AUTODESK INVENTOR PART (.ipt)
format: ipt  version: 2020 (Build 240168000, 168)  size: 176,128 bytes
history: native  units: mm
features: other x5, extrude x2
ambient origin geometry x8: Origin, YZ Plane, XZ Plane, XY Plane, X Axis, Y Axis, Z Axis, Center Point
bodies: Body1 (feature_tree)
feature tree (7):
  other  "Blocks"
  other  "OTICA"
  extrude  "Extrusion20"  Depth=40.0mm
  extrude  "Extrusion21"  Depth=0.685475mm
  other  "PENTAPRISMA"
  other  "PRISMA.ENTRADA"
  other  "PRISMA.ENTRADA:1"
